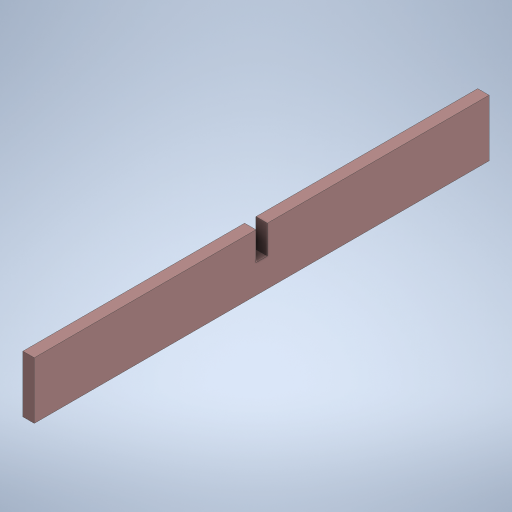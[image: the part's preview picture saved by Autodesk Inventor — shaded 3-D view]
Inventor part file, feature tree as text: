
AUTODESK INVENTOR PART (.ipt)
format: ipt  version: 2024.3 (Build 283343000, 343)  size: 247,808 bytes
history: native  units: mm
features: extrude x2, sketch x2
ambient origin geometry x8: Origin, YZ Plane, XZ Plane, XY Plane, X Axis, Y Axis, Z Axis, Center Point
bodies: Solid1 (feature_tree)
feature tree (4):
  extrude  "Extrusion1"  Depth=25.0mm
  extrude  "Extrusion2"  Depth=5.0mm
  sketch  "Sketch1"  dims[d0=200.0mm d1=25.0mm]
  sketch  "Sketch2"  dims[d2=5.0mm d3=0.0mm d4=5.0mm d5=5.0mm d6=0.0mm]
